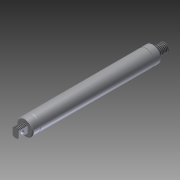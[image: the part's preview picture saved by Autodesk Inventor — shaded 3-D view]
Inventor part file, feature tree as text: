
AUTODESK INVENTOR PART (.ipt)
format: ipt  version: 2012 (Build 160160000, 160)  size: 156,672 bytes
history: native  units: in
note: dims shown in document units (in); Inventor stores cm internally (conversion verified against a paired STEP export)
features: extrude x7, sketch x3, thread x3, fillet x2, chamfer x2
ambient origin geometry x8: Origin, YZ Plane, XZ Plane, XY Plane, X Axis, Y Axis, Z Axis, Center Point
bodies: Solid1 (feature_tree)
feature tree (17):
  sketch  "Sketch1"  dims[d2=1.0in d3=1.125in d4=0.4167in]
  extrude  "Extrusion1"  Depth=1.125in
  fillet  "Fillet1"  Radius=0.4167in
  extrude  "Extrusion2"  Depth=0.4658in
  extrude  "Extrusion3"  Depth=0.3125in
  chamfer  "Chamfer1"  Distance=7.875in
  thread  "Thread1"  [1 undecoded]
  thread  "Thread2"  [1 undecoded]
  sketch  "Sketch2"  dims[d5=0.2083in d6=0.4658in]
  extrude  "Extrusion4"  Depth=1.125in TaperAngle=0.0deg
  extrude  "Extrusion5"  Depth=0.0625in TaperAngle=45.0deg
  fillet  "Fillet2"  Radius=1.0in
  extrude  "Extrusion6"  Depth=1.0in TaperAngle=0.0deg
  chamfer  "Chamfer2"  Distance=0.625in
  thread  "Thread3"  [1 undecoded]
  extrude  "Extrusion7"  Depth=0.25in
  sketch  "Sketch3"  dims[d7=0.2329in d8=0.3125in d10=7.875in d11=0.0in d12=0.0312in d13=0.5in d14=0.0in d15=1.125in d16=0.0in d17=0.0625in d18=0.125in d19=45.0deg d20=1.0in d21=0.0in d22=1.0in d23=0.0in d24=0.625in d25=0.3125in d26=0.25in d27=0.5in d28=0.0in d29=0.75in d30=0.0in d31=0.0075in d32=1.25in d33=0.0in d34=0.0625in d35=0.125in d36=45.0deg d37=1.0in d38=0.0in d39=0.25in d40=0.2329in d41=0.4658in d42=0.25in d43=1.0in d44=0.0in]
note: 3 required parameter values undecoded (feature->parameter linkage not recoverable at this tier; creation-order binding heuristic only, values carry confidence <= 0.55)
